# Revit family: WST-300-5B
name_source: partatom
category: Specialty Equipment
revit_build: Autodesk Revit 2016 (Build: 20150220_1215(x64)
units: mm (PartAtom-declared; Revit-internal decimal feet)

## family parameters
Always vertical = Yes
Cut with Voids When Loaded = No
Part Type = Normal
Room Calculation Point = No
Round Connector Dimension = Use Diameter
Shared = No
Work Plane-Based = No

## types (1)
- WST 300-5B
    A Radio_deposito = 335 mm  [stored 1.09908 ft]
    Agua caliente útil Tª salida 40ºC = 500 l
    Agua caliente útil Tª salida 45 ºC = 429 l
    Autor = 6d ingenieros
    Caudal máximo entrada agua fría = 30 l/min
    Clase de eficiencia energética de caldeo = B
    Conexión agua caliente = R1"
    Conexión agua fría = R1"
    Conexión recirculación = R3/4"
    Consumo térmico según DIN 4753 = 1,94 kWh/24 h
    Contenido = 300 l
    Contenido intercambiador = 8,8 l
    D Altura tanque = 1495 mm
    Description = Interacumulador de agua caliente sanitaria de 300 litros de capacidad, modelo WST 300-5B
    E = 80 mm  [stored 0.262467 ft]
    F = 318 mm  [stored 1.04331 ft]
    G = 722 mm  [stored 2.36877 ft]
    H = 903 mm  [stored 2.9626 ft]
    I = 1355 mm  [stored 4.44554 ft]
    J = 1850 mm  [stored 6.06955 ft]
    Manufacturer = BOSCH
    Model = WST 300-5B
    Peso en vacío = 105 kg
    PlasticArea = Bosch_160-160-160
    Potencia continua (80ºC imp./45ºC salida ACS/10ºC Suministro) = 36,5 kW
    Potencia máxima de calentamiento = 36,5 kW
    Presión de prueba máxima del agua caliente = 10 bar
    Presión de servicio máxima del agua potable = 10 bar
    Presión máxima intercambiador = 16 bar
    Presión nominal máxima = 7,8 bar
    Radio Impulsión acumulador = 13 mm
    Radio circulación = 10 mm  [stored 0.0328084 ft]
    Radio entrada agua fría = 13 mm
    Radio puerta = 345 mm  [stored 1.13189 ft]
    Radio retorno acumulador = 13 mm
    Radio salida agua caliente = 13 mm
    Radio sonda = 10 mm  [stored 0.0328084 ft]
    Superficie intercambiador = 1,3 m2
    Temperatura máxima intercambiador = 160 ºC
    Tiempo calentamiento con potencia nominal = 12 min
    Tª máxima agua caliente = 95 ºC
    URL = www.bosch-thermotechnology.com/es/es/comercial-e-industrial/ocs/stora-w-st--5-742030-p
    Versión = 1.0

note: [stored X ft] marks values corroborated as IEEE doubles in the binary element streams (Revit-internal decimal feet)

## geometry (parser evidence)
native form markers: Sweep x2
no freeform markers — native parametric forms only
